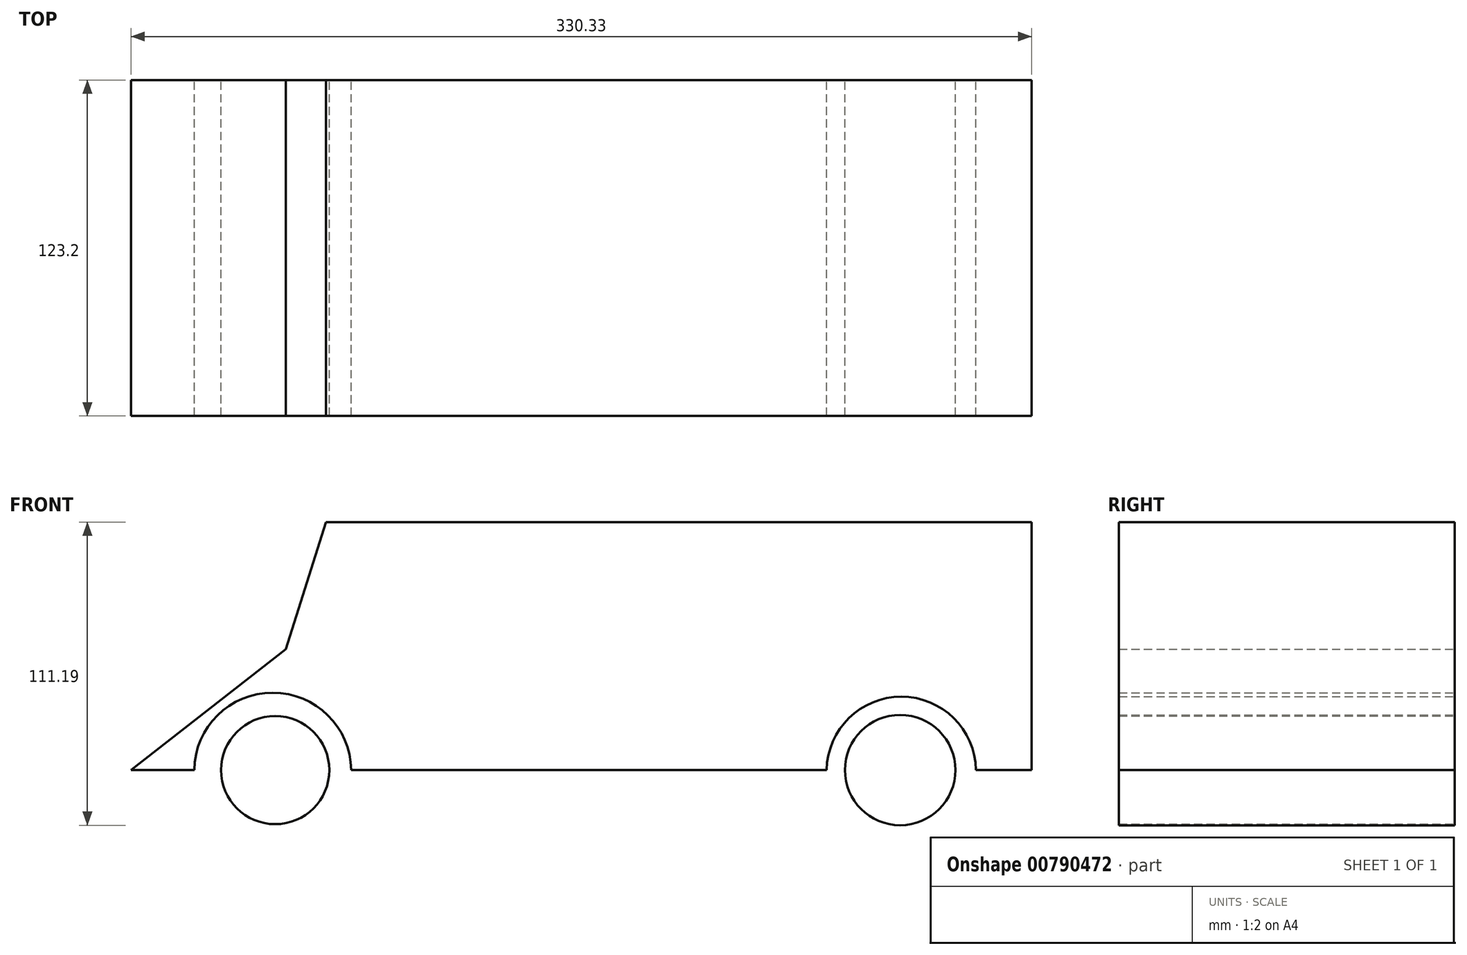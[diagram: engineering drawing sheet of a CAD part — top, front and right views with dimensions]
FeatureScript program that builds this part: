
annotation { "Feature Type Name" : "Feature", "Feature Type Description" : "" }
export const myFeature = defineFeature(function(context is Context, id is Id, definition is map)
    precondition{}
    {
        {
            var Q0;
            Q0=qCreatedBy(makeId("Front.planeOp"),FACE);
            var sketch = newSketch(context, id + "F0", { "sketchPlane" : qUnion([Q0])});
            skCircle(sketch, "E0", {"center": v(-114.72, -44.33) * mm, "radius": 19.85 * mm});
            skCircle(sketch, "E1", {"center": v(114.53, -44.33) * mm, "radius": 20.25 * mm});
            skArc(sketch, "E2", {"start": v(-86.83, -44.33) * mm, "mid": v(-115.62, -15.92) * mm, "end": v(-144.4, -44.33) * mm});
            skArc(sketch, "E3", {"start": v(142.33, -44.33) * mm, "mid": v(114.94, -17.38) * mm, "end": v(87.56, -44.33) * mm});
            skLineSegment(sketch, "E4", {"start": v(-86.83, -44.33) * mm, "end": v(87.56, -44.33) * mm});
            skLineSegment(sketch, "E5", {"start": v(-144.4, -44.33) * mm, "end": v(-167.6, -44.33) * mm});
            skLineSegment(sketch, "E6", {"start": v(-167.6, -44.33) * mm, "end": v(-110.86, 0) * mm});
            skLineSegment(sketch, "E7", {"start": v(-110.86, 0) * mm, "end": v(-96.05, 46.62) * mm});
            skLineSegment(sketch, "E8", {"start": v(-96.05, 46.62) * mm, "end": v(162.73, 46.62) * mm});
            skLineSegment(sketch, "E9", {"start": v(162.73, 46.62) * mm, "end": v(162.73, -44.33) * mm});
            skLineSegment(sketch, "E10", {"start": v(162.73, -44.33) * mm, "end": v(142.33, -44.33) * mm});
            skSolve(sketch);
        }
        {
            var Q0;
            Q0 = qSketchRegion(id + "F0", true);
            extrude(context, id + "F1", {"entities" : qUnion([Q0]), "depth" : 123.2 * mm, "offsetDistance" : 25 * mm});
        }
    });
